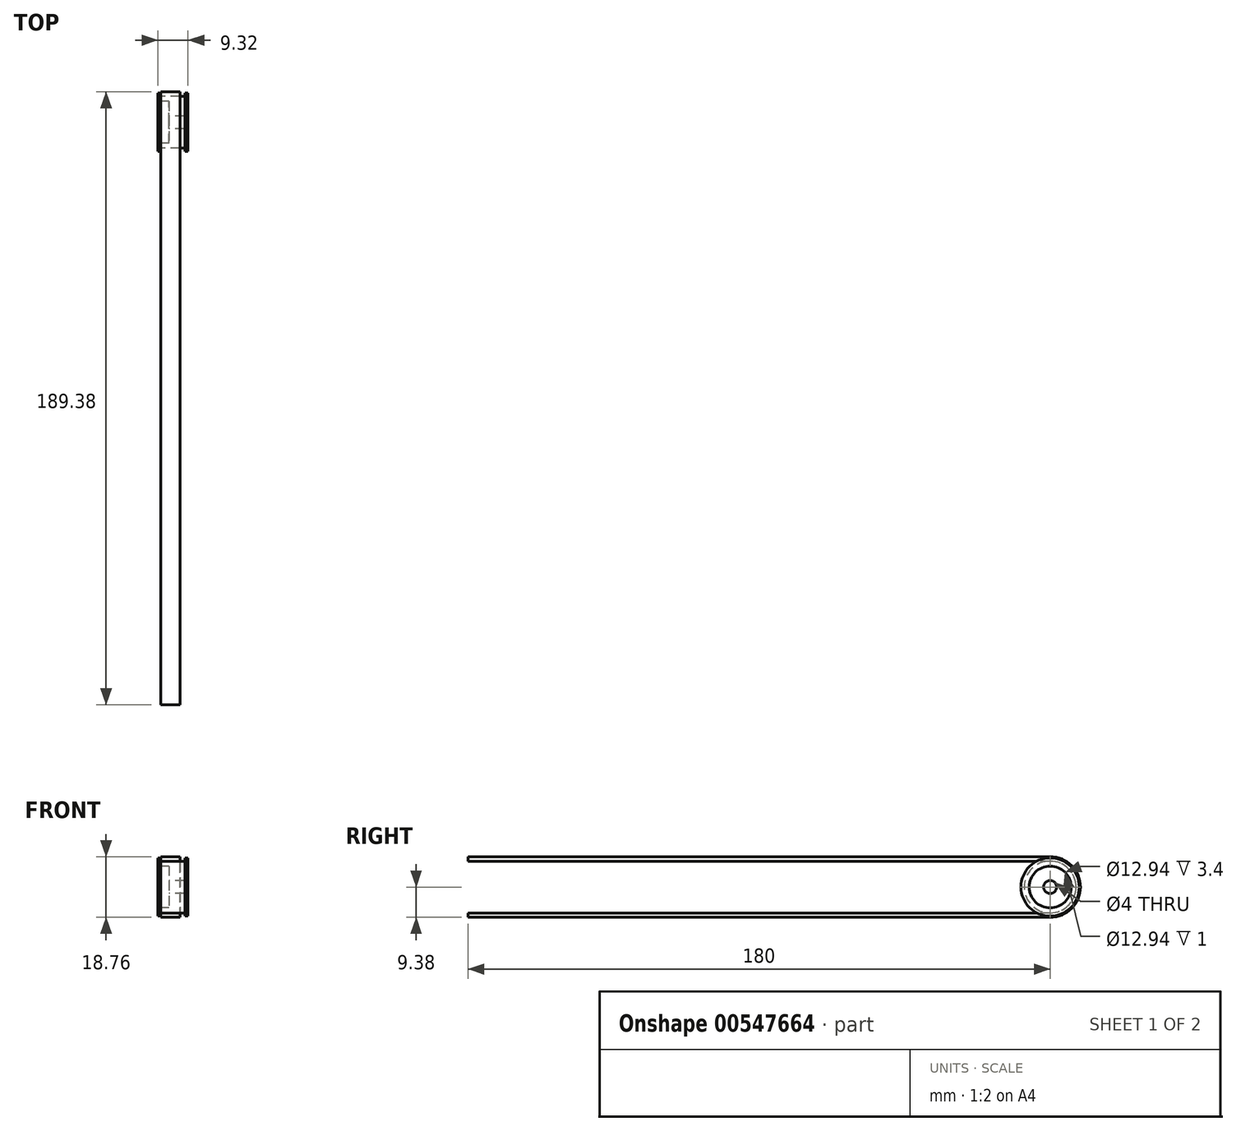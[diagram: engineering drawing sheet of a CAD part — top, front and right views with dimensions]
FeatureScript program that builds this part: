
annotation { "Feature Type Name" : "Feature", "Feature Type Description" : "" }
export const myFeature = defineFeature(function(context is Context, id is Id, definition is map)
    precondition{}
    {
        {
            var Q0;
            Q0=qCreatedBy(makeId("Front.planeOp"),FACE);
            var sketch = newSketch(context, id + "F0", { "sketchPlane" : qUnion([Q0])});
            skLineSegment(sketch, "E0", {"start": v(0, 0) * mm, "end": v(9.32, 0) * mm, "construction": true});
            skLineSegment(sketch, "E1", {"start": v(0, 6.47) * mm, "end": v(0, 9) * mm});
            skLineSegment(sketch, "E2", {"start": v(0, 9) * mm, "end": v(0.91, 9) * mm});
            skLineSegment(sketch, "E3", {"start": v(0.91, 9) * mm, "end": v(0.91, 8) * mm});
            skLineSegment(sketch, "E4", {"start": v(0.91, 8) * mm, "end": v(8.4, 8) * mm});
            skLineSegment(sketch, "E5", {"start": v(8.4, 8) * mm, "end": v(8.4, 9) * mm});
            skLineSegment(sketch, "E6", {"start": v(8.4, 9) * mm, "end": v(9.32, 9) * mm});
            skLineSegment(sketch, "E7", {"start": v(9.32, 9) * mm, "end": v(9.32, 6.47) * mm});
            skLineSegment(sketch, "E8", {"start": v(9.32, 6.47) * mm, "end": v(8.32, 6.47) * mm});
            skLineSegment(sketch, "E9", {"start": v(8.32, 6.47) * mm, "end": v(8.32, 2) * mm});
            skLineSegment(sketch, "E10", {"start": v(3.4, 6.47) * mm, "end": v(0, 6.47) * mm});
            skPoint(sketch, "E11", {"position": v(4.66, 0) * mm});
            skPoint(sketch, "E12", {"position": v(4.66, 2) * mm});
            skPoint(sketch, "E13", {"position": v(4.66, 8) * mm});
            skLineSegment(sketch, "E14", {"start": v(3.4, 6.47) * mm, "end": v(3.4, 2) * mm});
            skLineSegment(sketch, "E15", {"start": v(3.4, 2) * mm, "end": v(8.32, 2) * mm});
            skSolve(sketch);
        }
        {
            var Q0;
            Q0=qSketchRegion(id+"F0",true);
            var Q1;
            Q1=sQuery(id+"F0.wireOp",EDGE,"E0");
            revolve(context, id + "F1", {"entities" : qUnion([Q0]), "axis" : qUnion([Q1]), "revolveType" : RevolveType.FULL});
        }
        {
            var Q0;
            Q0=makeQuery(id+"F1.opRevolve","SWEPT_FACE",FACE,{"disambiguationData":[OSD([sQuery(id+"F0.wireOp",EDGE,"E3")])]});
            var sketch = newSketch(context, id + "F2", { "sketchPlane" : qUnion([Q0])});
            skCircle(sketch, "E16.0", {"center": v(0, 0) * mm, "radius": 8 * mm, "construction": true});
            skLineSegment(sketch, "E17", {"start": v(0, -8) * mm, "end": v(-180, -8) * mm});
            skLineSegment(sketch, "E18", {"start": v(-180, -8) * mm, "end": v(-180, -9.38) * mm});
            skArc(sketch, "E19", {"start": v(0, -8) * mm, "mid": v(8, 0) * mm, "end": v(0, 8) * mm});
            skLineSegment(sketch, "E20", {"start": v(-180, -9.38) * mm, "end": v(0, -9.38) * mm});
            skArc(sketch, "E21", {"start": v(0, -9.38) * mm, "mid": v(9.38, 0) * mm, "end": v(0, 9.38) * mm});
            skLineSegment(sketch, "E22", {"start": v(0, 8) * mm, "end": v(-180, 8) * mm});
            skLineSegment(sketch, "E23", {"start": v(-180, 8) * mm, "end": v(-180, 9.38) * mm});
            skLineSegment(sketch, "E24", {"start": v(-180, 9.38) * mm, "end": v(0, 9.38) * mm});
            skSolve(sketch);
        }
        {
            var Q0;
            Q0=qSketchRegion(id+"F2",true);
            extrude(context, id + "F3", {"entities" : qUnion([Q0]), "depth" : 6 * mm});
        }
    });
